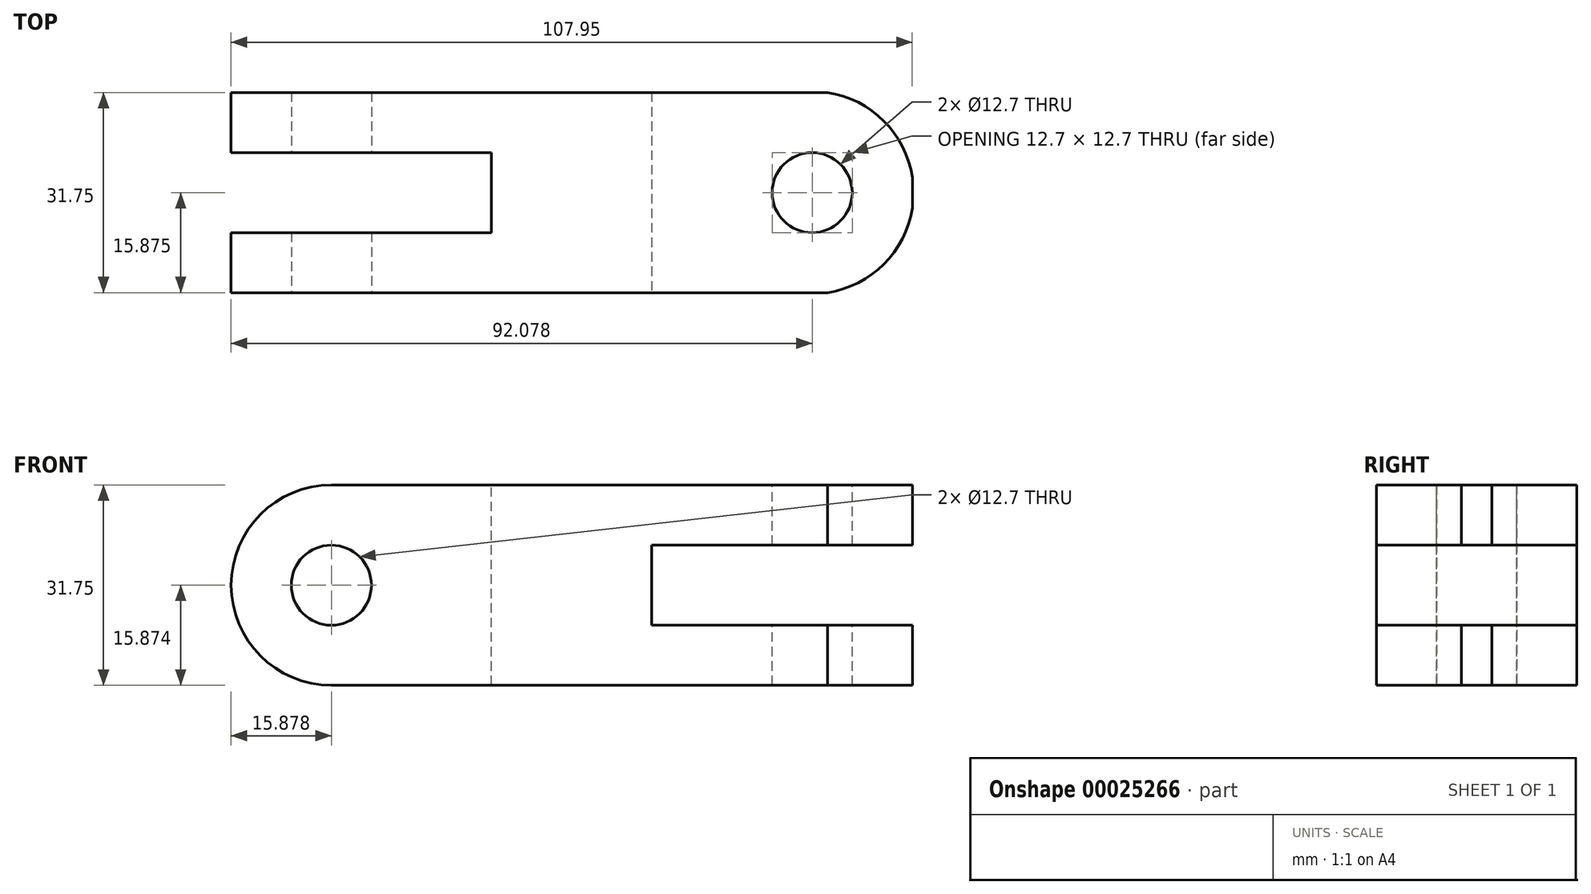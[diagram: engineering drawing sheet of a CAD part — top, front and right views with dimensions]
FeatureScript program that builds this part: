
annotation { "Feature Type Name" : "Feature", "Feature Type Description" : "" }
export const myFeature = defineFeature(function(context is Context, id is Id, definition is map)
    precondition{}
    {
        {
            var Q0;
            Q0=qCreatedBy(makeId("Front.planeOp"),FACE);
            var sketch = newSketch(context, id + "F0", { "sketchPlane" : qUnion([Q0])});
            skLineSegment(sketch, "E0.bottom", {"start": v(-65.58, 33.58) * mm, "end": v(42.37, 33.58) * mm});
            skLineSegment(sketch, "E0.top", {"start": v(-65.58, 1.83) * mm, "end": v(42.37, 1.83) * mm});
            skLineSegment(sketch, "E0.left", {"start": v(-65.58, 33.58) * mm, "end": v(-65.58, 1.83) * mm});
            skLineSegment(sketch, "E0.right", {"start": v(42.37, 33.58) * mm, "end": v(42.37, 1.83) * mm});
            skSolve(sketch);
        }
        {
            var Q0;
            Q0=makeQuery(id+"F0.imprint","IMPRINT",FACE,{"disambiguationData":[TD([[makeQuery(id+"F0.imprint","IMPRINT",EDGE,{"derivedFrom":sQuery(id+"F0.wireOp",EDGE,"E0.bottom")}),-1.0]])]});
            extrude(context, id + "F1", {"entities" : qUnion([Q0]), "depth" : 31.75 * mm});
        }
        {
            var Q0;
            Q0=makeQuery(id+"F1.opExtrude","CAP_FACE",FACE,{"disambiguationData":[OSD([sQuery(id+"F0.wireOp",EDGE,"E0.bottom"),sQuery(id+"F0.wireOp",EDGE,"E0.top"),sQuery(id+"F0.wireOp",EDGE,"E0.left"),sQuery(id+"F0.wireOp",EDGE,"E0.right")])],"isStart":false});
            var sketch = newSketch(context, id + "F2", { "sketchPlane" : qUnion([Q0])});
            skLineSegment(sketch, "E1.0", {"start": v(-49.7, 33.58) * mm, "end": v(-49.7, 1.83) * mm, "construction": true});
            skArc(sketch, "E2", {"start": v(-49.7, 33.58) * mm, "mid": v(-65.58, 17.7) * mm, "end": v(-49.7, 1.83) * mm});
            skCircle(sketch, "E3", {"center": v(-49.7, 17.7) * mm, "radius": 6.35 * mm});
            skLineSegment(sketch, "E4.0", {"start": v(-65.58, 24.05) * mm, "end": v(-64.25, 24.05) * mm, "construction": true});
            skLineSegment(sketch, "E5.0", {"start": v(-65.58, 11.35) * mm, "end": v(-64.25, 11.35) * mm, "construction": true});
            skLineSegment(sketch, "E6.0", {"start": v(1.1, 24.05) * mm, "end": v(1.1, 11.35) * mm});
            skLineSegment(sketch, "E7.trimOffspring", {"start": v(1.1, 11.35) * mm, "end": v(42.37, 11.35) * mm});
            skLineSegment(sketch, "E8.trimOffspring", {"start": v(1.1, 24.05) * mm, "end": v(42.37, 24.05) * mm});
            skSolve(sketch);
        }
        {
            var Q0;
            Q0=makeQuery(id+"F2.imprint","IMPRINT",FACE,{"disambiguationData":[TD([[makeQuery(id+"F2.imprint","IMPRINT",EDGE,{"derivedFrom":sQuery(id+"F2.wireOp",EDGE,"E3")}),1.0]])]});
            var Q1;
            {var subQ1=sQuery(id+"F2.wireOp",EDGE,"E2");var subQ3=makeQuery(id+"F1.opExtrude","CAP_EDGE",EDGE,{"disambiguationData":[OSD([sQuery(id+"F0.wireOp",EDGE,"E0.bottom")])],"isStart":false});var subQ5=makeQuery(id+"F2.imprint","INTERSECT",VERTEX,{"derivedFrom":[subQ3,subQ1]});Q1=makeQuery(id+"F2.imprint","IMPRINT",FACE,{"disambiguationData":[TD([[makeQuery(id+"F2.imprint","IMPRINT",EDGE,{"disambiguationData":[TD([[subQ5,-1.0]])],"derivedFrom":subQ1}),-1.0]])]});}
            var Q2;
            {var subQ1=sQuery(id+"F2.wireOp",EDGE,"E2");var subQ3=makeQuery(id+"F1.opExtrude","CAP_EDGE",EDGE,{"disambiguationData":[OSD([sQuery(id+"F0.wireOp",EDGE,"E0.top")])],"isStart":false});var subQ5=makeQuery(id+"F2.imprint","INTERSECT",VERTEX,{"derivedFrom":[subQ3,subQ1]});Q2=makeQuery(id+"F2.imprint","IMPRINT",FACE,{"disambiguationData":[TD([[makeQuery(id+"F2.imprint","IMPRINT",EDGE,{"disambiguationData":[TD([[subQ5,1.0]])],"derivedFrom":subQ1}),-1.0]])]});}
            var Q3;
            Q3=makeQuery(id+"F2.imprint","IMPRINT",FACE,{"disambiguationData":[TD([[makeQuery(id+"F2.imprint","IMPRINT",EDGE,{"derivedFrom":sQuery(id+"F2.wireOp",EDGE,"E6.0")}),1.0]])]});
            extrude(context, id + "F3", {"entities" : qUnion([Q0, Q1, Q2, Q3]), "operationType" : NewBodyOperationType.REMOVE, "endBound" : BoundingType.THROUGH_ALL, "oppositeDirection" : true, "depth" : 25.4 * mm});
        }
        {
            var Q0;
            Q0=makeQuery(id+"F1.opExtrude","SWEPT_FACE",FACE,{"disambiguationData":[OSD([sQuery(id+"F0.wireOp",EDGE,"E0.bottom")])]});
            var sketch = newSketch(context, id + "F4", { "sketchPlane" : qUnion([Q0])});
            skLineSegment(sketch, "E9.0", {"start": v(-24.3, -9.53) * mm, "end": v(-24.3, -22.22) * mm});
            skLineSegment(sketch, "E10.0", {"start": v(-49.7, -22.23) * mm, "end": v(-65.58, -22.23) * mm});
            skLineSegment(sketch, "E11.0", {"start": v(-49.7, -22.23) * mm, "end": v(-24.3, -22.23) * mm});
            skLineSegment(sketch, "E12.0", {"start": v(-49.7, -9.53) * mm, "end": v(-24.3, -9.53) * mm});
            skLineSegment(sketch, "E13.0", {"start": v(-49.7, -9.53) * mm, "end": v(-65.58, -9.53) * mm});
            skLineSegment(sketch, "E14.0", {"start": v(26.5, -31.93) * mm, "end": v(26.5, 0.18) * mm});
            skArc(sketch, "E15", {"start": v(26.5, -31.93) * mm, "mid": v(42.56, -15.88) * mm, "end": v(26.5, 0.18) * mm});
            skCircle(sketch, "E16", {"center": v(26.5, -15.88) * mm, "radius": 6.35 * mm});
            skPoint(sketch, "E17.orphan", {"position": v(26.5, 0) * mm});
            skPoint(sketch, "E18.orphan", {"position": v(26.5, -31.75) * mm});
            skLineSegment(sketch, "E19.trimOffspring", {"start": v(26.5, -22.23) * mm, "end": v(41.25, -22.23) * mm});
            skLineSegment(sketch, "E20", {"start": v(-65.58, -9.53) * mm, "end": v(-65.58, -22.23) * mm});
            skSolve(sketch);
        }
        {
            var Q0;
            Q0=makeQuery(id+"F4.imprint","IMPRINT",FACE,{"disambiguationData":[TD([[makeQuery(id+"F4.imprint","IMPRINT",EDGE,{"derivedFrom":sQuery(id+"F4.wireOp",EDGE,"E9.0")}),-1.0]])]});
            var Q1;
            {var subQ0=sQuery(id+"F4.wireOp",EDGE,"E16");var subQ1=sQuery(id+"F4.wireOp",EDGE,"E14.0");var subQ2=makeQuery(id+"F4.imprint","INTERSECT",VERTEX,{"derivedFrom":[subQ1,subQ0]});Q1=makeQuery(id+"F4.imprint","IMPRINT",FACE,{"disambiguationData":[TD([[makeQuery(id+"F4.imprint","IMPRINT",EDGE,{"disambiguationData":[TD([[subQ2,1.0]])],"derivedFrom":subQ1}),-1.0]])]});}
            var Q2;
            {var subQ0=sQuery(id+"F4.wireOp",EDGE,"E16");var subQ1=sQuery(id+"F4.wireOp",EDGE,"E14.0");var subQ2=makeQuery(id+"F4.imprint","INTERSECT",VERTEX,{"derivedFrom":[subQ1,subQ0]});Q2=makeQuery(id+"F4.imprint","IMPRINT",FACE,{"disambiguationData":[TD([[makeQuery(id+"F4.imprint","IMPRINT",EDGE,{"disambiguationData":[TD([[subQ2,1.0]])],"derivedFrom":subQ1}),1.0]])]});}
            var Q3;
            {var subQ0=sQuery(id+"F0.wireOp",EDGE,"E0.bottom");var subQ1=makeQuery(id+"F1.opExtrude","CAP_EDGE",EDGE,{"disambiguationData":[OSD([subQ0])],"isStart":true});var subQ2=sQuery(id+"F4.wireOp",EDGE,"E15");var subQ3=makeQuery(id+"F4.imprint","INTERSECT",VERTEX,{"derivedFrom":[subQ1,subQ2]});Q3=makeQuery(id+"F4.imprint","IMPRINT",FACE,{"disambiguationData":[TD([[makeQuery(id+"F4.imprint","IMPRINT",EDGE,{"disambiguationData":[TD([[subQ3,1.0]])],"derivedFrom":subQ2}),-1.0]])]});}
            var Q4;
            {var subQ2=sQuery(id+"F4.wireOp",EDGE,"E15");var subQ7=makeQuery(id+"F4.imprint","INTERSECT",VERTEX,{"derivedFrom":[subQ2,sQuery(id+"F4.wireOp",EDGE,"E19.trimOffspring")]});Q4=makeQuery(id+"F4.imprint","IMPRINT",FACE,{"disambiguationData":[TD([[makeQuery(id+"F4.imprint","IMPRINT",EDGE,{"disambiguationData":[TD([[subQ7,1.0]])],"derivedFrom":subQ2}),-1.0]])]});}
            var Q5;
            {var subQ2=sQuery(id+"F4.wireOp",EDGE,"E10.0");Q5=makeQuery(id+"F4.imprint","IMPRINT",FACE,{"disambiguationData":[TD([[makeQuery(id+"F4.imprint","IMPRINT",EDGE,{"derivedFrom":subQ2}),-1.0]])]});}
            extrude(context, id + "F5", {"entities" : qUnion([Q0, Q1, Q2, Q3, Q4, Q5]), "operationType" : NewBodyOperationType.REMOVE, "endBound" : BoundingType.THROUGH_ALL, "oppositeDirection" : true, "depth" : 25.4 * mm});
        }
    });
